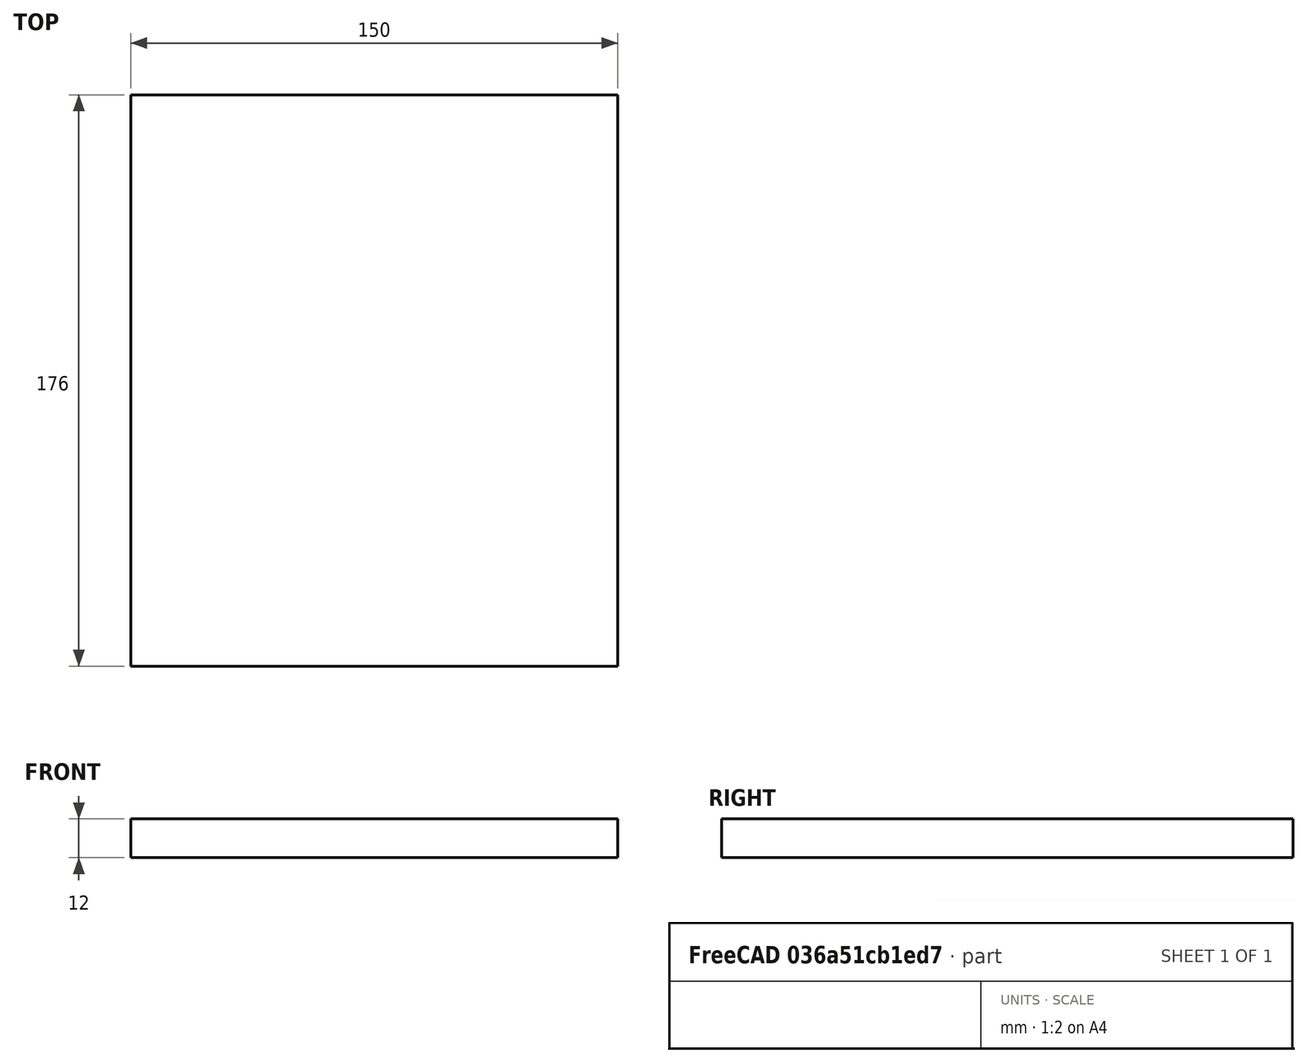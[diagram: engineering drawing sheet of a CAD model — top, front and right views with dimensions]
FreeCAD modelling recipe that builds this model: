
FCSTD DOCUMENT  (FreeCAD 0.16R6703 (Git))
Label: box2_sides
License: All rights reserved
LicenseURL: http://en.wikipedia.org/wiki/All_rights_reserved
objects: Drawing::FeatureViewPython×3, Drawing::FeatureViewPart×2, Sketcher::SketchObject×1, PartDesign::Pad×1, Drawing::FeaturePage×1
note: 3 computed .brp shape members not serialized (recipe doc carries the construction recipe); baked Part::Feature solids carry a one-line shape summary decoded from their .brp

FEATURE [Sketcher::SketchObject] Sketch
  expr: Constraints[10] = 200 - 2 * 12
  sketch-geometry (4):
    g0: LineSegment StartX=0 StartY=0 StartZ=0 EndX=150 EndY=0 EndZ=0
    g1: LineSegment StartX=150 StartY=0 StartZ=0 EndX=150 EndY=176 EndZ=0
    g2: LineSegment StartX=150 StartY=176 StartZ=0 EndX=0 EndY=176 EndZ=0
    g3: LineSegment StartX=0 StartY=176 StartZ=0 EndX=0 EndY=0 EndZ=0
  constraints (11):
    c: Coincident(g0,g1)
    c: Coincident(g1,g2)
    c: Coincident(g2,g3)
    c: Coincident(g3,g0)
    c: Horizontal(g0)
    c: Horizontal(g2)
    c: Vertical(g1)
    c: Vertical(g3)
    c: Coincident(g0,g-1)
    c: Distance(g2) = 150
    c: Distance(g3) = 176
FEATURE [PartDesign::Pad] Pad
  Length = 12
  Length2 = 100
  Sketch = -> Sketch
  Type = 0
FEATURE [Drawing::FeatureViewPart] Ortho  label="Ortho_0_0"
  Direction = (1,0,0)
  HiddenWidth = 0.15
  LineWidth = 0.35
  Rotation = -90
  ShowHiddenLines = false
  ShowSmoothLines = false
  Source = -> Pad
  Tolerance = 0.05
  ViewResult = <g id="Ortho_0_0"\n   transform="rotate(-90,122,40.3333) translate(122,40.3333) scale(1,1)"\n  >\n<g   stroke="rgb(0, 0, 0)"\n   stroke-width="0.35"\n   stroke-linecap="butt"\n   stroke-linejoin="miter"\n   fill="none"\n   transform="scale(1,-1)"\n  >\n<path id= "1" d=" M 0 0 L 12 0 " />\n<path id= "2" d=" M 0 -176 L 12 -176 " />\n<path id= "3" d=" M 0 0 L 0 -176 " />\n<path id= "4" d=" M 12 0 L 12 -176 " />\n</g>\n</g>
  Visible = true
  X = 122
  Y = 40.3333
FEATURE [Drawing::FeatureViewPart] Ortho001  label="Ortho_0_-1"
  Direction = (0,0,-1)
  HiddenWidth = 0.15
  LineWidth = 0.35
  Rotation = 90
  ShowHiddenLines = false
  ShowSmoothLines = false
  Source = -> Pad
  Tolerance = 0.05
  ViewResult = <g id="Ortho_0_-1"\n   transform="rotate(90,122,208.667) translate(122,208.667) scale(1,1)"\n  >\n<g   stroke="rgb(0, 0, 0)"\n   stroke-width="0.35"\n   stroke-linecap="butt"\n   stroke-linejoin="miter"\n   fill="none"\n   transform="scale(1,-1)"\n  >\n<path id= "1" d=" M 0 0 L -150 0 " />\n<path id= "2" d=" M -150 0 L -150 176 " />\n<path id= "3" d=" M -150 176 L 0 176 " />\n<path id= "4" d=" M 0 176 L 0 0 " />\n</g>\n</g>
  Visible = true
  X = 122
  Y = 208.667
FEATURE [Drawing::FeatureViewPython] dim001  # drawing view (typed FeaturePython)
  Rotation = 0
  ViewResult = <g> \n  <line x1="120.000000" y1="208.667000" x2="100.679319" y2="208.667000" style="stroke:rgb(0,0,255);stroke-width:0.50" />\n<line x1="120.000000" y1="58.667000" x2="100.679319" y2="58.667000" style="stroke:rgb(0,0,255);stroke-width:0.50" />\n<line x1="101.679319" y1="208.667000" x2="101.679319" y2="58.667000" style="stroke:rgb(0,0,255);stroke-width:0.50" /> \n  <polygon points="101.679319,58.667000 100.679319,61.667000 101.679319,62.667000 102.679319,61.667000" style="fill:rgb(0,0,255);stroke:rgb(0,0,255);stroke-width:0" /><polygon points="101.679319,208.667000 102.679319,205.667000 101.679319,204.667000 100.679319,205.667000" style="fill:rgb(0,0,255);stroke:rgb(0,0,255);stroke-width:0" /> \n  <text x="99.679319" y="133.667000" font-family="inherit" font-size="7" fill="rgb(0,0,255)" text-anchor="middle" transform="rotate(-90.000000 99.679319,133.667000)" >150</text> </g>
  Visible = true
  X = 0
  Y = 0
  arrowL1 = 3
  arrowL2 = 1
  arrowW = 2
  arrow_scheme = 0
  autoPlaceOffset = 2
  autoPlaceText = true
  click1_x = 101.679
  click1_y = 83.9032
  click2_x = 101.679
  click2_y = 83.9032
  comma_decimal_place = false
  dimension_line_overshoot = 1
  gap_datum_points = 2
  halfDimension_linear = false
  lineColor = rgb(0,0,255)
  strokeWidth = 0.5
  textFormat_linear = %(value)3.3f
  textRenderer_color = rgb(0,0,255)
  textRenderer_family = inherit
  textRenderer_size = 7
  unit_custom_scale = 0.8
  unit_scheme = 0
FEATURE [Drawing::FeatureViewPython] dim002  # drawing view (typed FeaturePython)
  Rotation = 0
  ViewResult = <g> \n  <line x1="120.000000" y1="40.333300" x2="98.546187" y2="40.333300" style="stroke:rgb(0,0,255);stroke-width:0.50" />\n<line x1="120.000000" y1="28.333300" x2="98.546187" y2="28.333300" style="stroke:rgb(0,0,255);stroke-width:0.50" />\n<line x1="99.546187" y1="40.333300" x2="99.546187" y2="28.333300" style="stroke:rgb(0,0,255);stroke-width:0.50" /> \n  <polygon points="99.546187,28.333300 98.546187,31.333300 99.546187,32.333300 100.546187,31.333300" style="fill:rgb(0,0,255);stroke:rgb(0,0,255);stroke-width:0" /><polygon points="99.546187,40.333300 100.546187,37.333300 99.546187,36.333300 98.546187,37.333300" style="fill:rgb(0,0,255);stroke:rgb(0,0,255);stroke-width:0" /> \n  <text x="97.546187" y="34.333300" font-family="inherit" font-size="7" fill="rgb(0,0,255)" text-anchor="middle" transform="rotate(-90.000000 97.546187,34.333300)" >12</text> </g>
  Visible = true
  X = 0
  Y = 0
  arrowL1 = 3
  arrowL2 = 1
  arrowW = 2
  arrow_scheme = 0
  autoPlaceOffset = 2
  autoPlaceText = true
  click1_x = 99.5462
  click1_y = 35.9077
  click2_x = 99.5462
  click2_y = 35.9077
  comma_decimal_place = false
  dimension_line_overshoot = 1
  gap_datum_points = 2
  halfDimension_linear = false
  lineColor = rgb(0,0,255)
  strokeWidth = 0.5
  textFormat_linear = %(value)3.3f
  textRenderer_color = rgb(0,0,255)
  textRenderer_family = inherit
  textRenderer_size = 7
  unit_custom_scale = 0.8
  unit_scheme = 0
FEATURE [Drawing::FeatureViewPython] dim003  # drawing view (typed FeaturePython)
  Rotation = 0
  ViewResult = <g> \n  <line x1="298.000000" y1="210.667000" x2="298.000000" y2="219.646088" style="stroke:rgb(0,0,255);stroke-width:0.50" />\n<line x1="122.000000" y1="210.667000" x2="122.000000" y2="219.646088" style="stroke:rgb(0,0,255);stroke-width:0.50" />\n<line x1="298.000000" y1="218.646088" x2="122.000000" y2="218.646088" style="stroke:rgb(0,0,255);stroke-width:0.50" /> \n  <polygon points="122.000000,218.646088 125.000000,219.646088 126.000000,218.646088 125.000000,217.646088" style="fill:rgb(0,0,255);stroke:rgb(0,0,255);stroke-width:0" /><polygon points="298.000000,218.646088 295.000000,217.646088 294.000000,218.646088 295.000000,219.646088" style="fill:rgb(0,0,255);stroke:rgb(0,0,255);stroke-width:0" /> \n  <text x="210.000000" y="216.646088" font-family="inherit" font-size="7" fill="rgb(0,0,255)" text-anchor="middle" transform="rotate(0.000000 210.000000,216.646088)" >176</text> </g>
  Visible = true
  X = 0
  Y = 0
  arrowL1 = 3
  arrowL2 = 1
  arrowW = 2
  arrow_scheme = 0
  autoPlaceOffset = 2
  autoPlaceText = true
  click1_x = 150.741
  click1_y = 218.646
  click2_x = 150.741
  click2_y = 218.646
  comma_decimal_place = false
  dimension_line_overshoot = 1
  gap_datum_points = 2
  halfDimension_linear = false
  lineColor = rgb(0,0,255)
  strokeWidth = 0.5
  textFormat_linear = %(value)3.3f
  textRenderer_color = rgb(0,0,255)
  textRenderer_family = inherit
  textRenderer_size = 7
  unit_custom_scale = 0.8
  unit_scheme = 0
FEATURE [Drawing::FeaturePage] Page
  EditableTexts = AUTHOR NAME | CREATION DATE | SUPERVISOR NAME | CHECK DATE | SCALE | WEIGHT | NUMBER | SHEET | Box 2 Sides | SUBTITLE
  Group = -> [Ortho,Ortho001,dim001,dim002,dim003]
